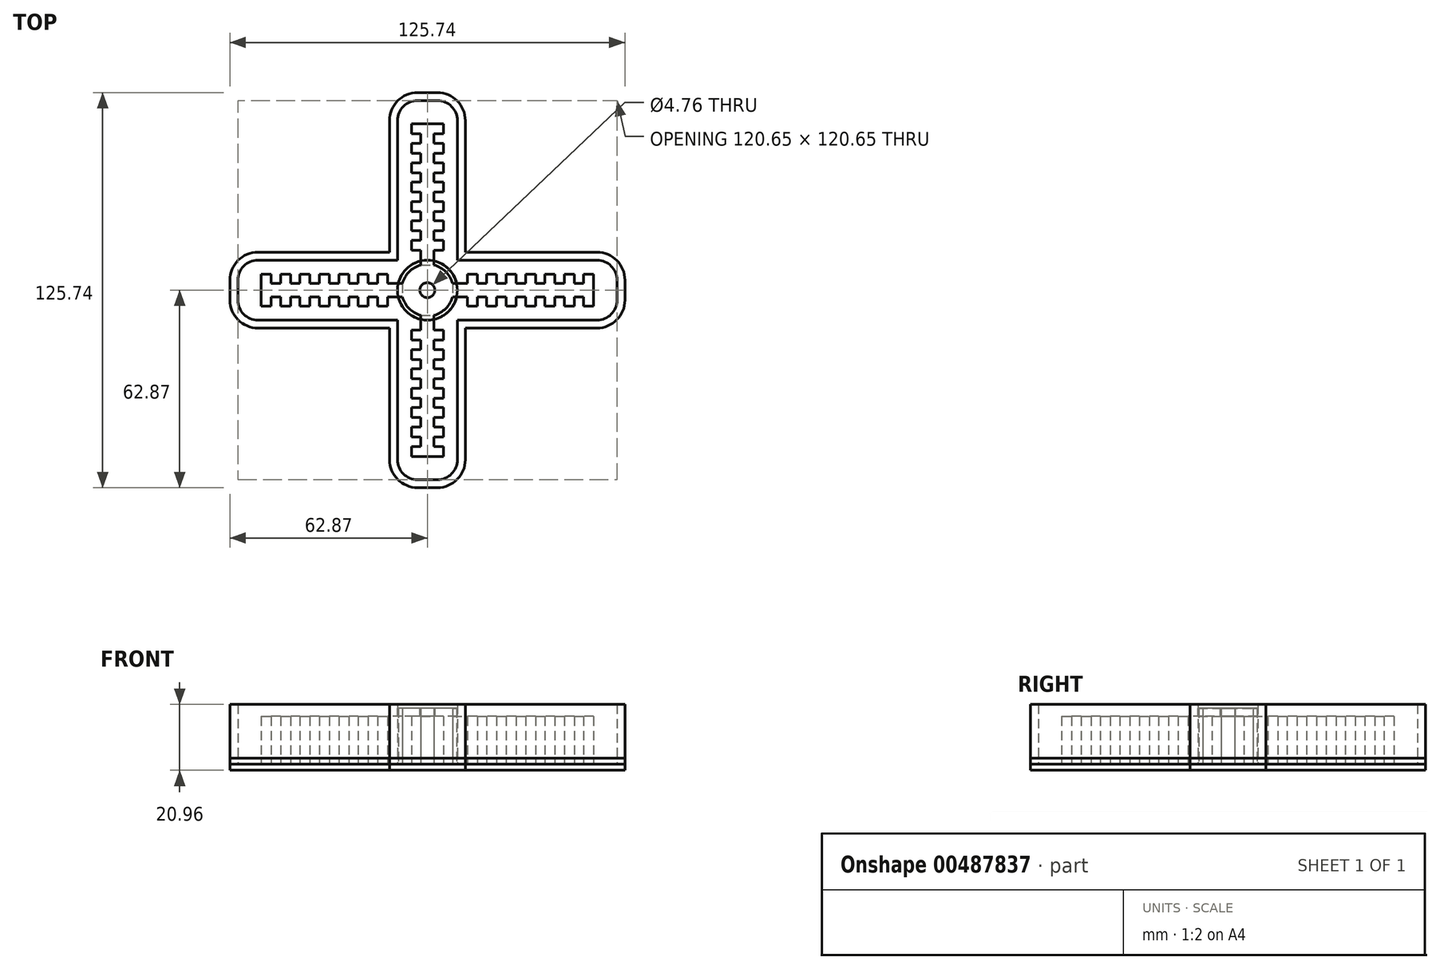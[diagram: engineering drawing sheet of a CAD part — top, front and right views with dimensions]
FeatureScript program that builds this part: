
annotation { "Feature Type Name" : "Feature", "Feature Type Description" : "" }
export const myFeature = defineFeature(function(context is Context, id is Id, definition is map)
    precondition{}
    {
        {
            var Q0;
            Q0=qCreatedBy(makeId("Top.planeOp"),FACE);
            var sketch = newSketch(context, id + "F0", { "sketchPlane" : qUnion([Q0])});
            skArc(sketch, "E0", {"start": v(-2.12, 9.29) * mm, "mid": v(-6.74, 6.74) * mm, "end": v(-9.29, 2.12) * mm});
            skLineSegment(sketch, "E1", {"start": v(-3.18, 60.33) * mm, "end": v(3.17, 60.33) * mm});
            skLineSegment(sketch, "E2.0", {"start": v(2.12, 7.98) * mm, "end": v(2.12, 12.7) * mm});
            skLineSegment(sketch, "E3.0", {"start": v(-2.12, 7.98) * mm, "end": v(-2.12, 12.7) * mm});
            skLineSegment(sketch, "E4", {"start": v(-5.08, 15.88) * mm, "end": v(-2.12, 15.88) * mm});
            skLineSegment(sketch, "E5", {"start": v(5.08, 15.88) * mm, "end": v(5.08, 12.7) * mm});
            skLineSegment(sketch, "E6", {"start": v(5.08, 12.7) * mm, "end": v(2.12, 12.7) * mm});
            skLineSegment(sketch, "E7", {"start": v(-5.08, 12.7) * mm, "end": v(-5.08, 15.88) * mm});
            skLineSegment(sketch, "E8.0.1.0", {"start": v(-5.08, 22.05) * mm, "end": v(-2.12, 22.05) * mm});
            skLineSegment(sketch, "E8.0.1.1", {"start": v(-5.08, 18.87) * mm, "end": v(-5.08, 22.05) * mm});
            skLineSegment(sketch, "E8.0.1.2", {"start": v(5.08, 18.87) * mm, "end": v(2.12, 18.87) * mm});
            skLineSegment(sketch, "E8.0.1.3", {"start": v(5.08, 22.05) * mm, "end": v(5.08, 18.87) * mm});
            skLineSegment(sketch, "E8.0.2.0", {"start": v(-5.08, 28.22) * mm, "end": v(-2.12, 28.22) * mm});
            skLineSegment(sketch, "E8.0.2.1", {"start": v(-5.08, 25.04) * mm, "end": v(-5.08, 28.22) * mm});
            skLineSegment(sketch, "E8.0.2.2", {"start": v(5.08, 25.04) * mm, "end": v(2.12, 25.04) * mm});
            skLineSegment(sketch, "E8.0.2.3", {"start": v(5.08, 28.22) * mm, "end": v(5.08, 25.04) * mm});
            skLineSegment(sketch, "E8.0.3.0", {"start": v(-5.08, 34.4) * mm, "end": v(-2.12, 34.4) * mm});
            skLineSegment(sketch, "E8.0.3.1", {"start": v(-5.08, 31.22) * mm, "end": v(-5.08, 34.4) * mm});
            skLineSegment(sketch, "E8.0.3.2", {"start": v(5.08, 31.22) * mm, "end": v(2.12, 31.22) * mm});
            skLineSegment(sketch, "E8.0.3.3", {"start": v(5.08, 34.4) * mm, "end": v(5.08, 31.22) * mm});
            skLineSegment(sketch, "E8.0.4.0", {"start": v(-5.08, 40.56) * mm, "end": v(-2.12, 40.56) * mm});
            skLineSegment(sketch, "E8.0.4.1", {"start": v(-5.08, 37.39) * mm, "end": v(-5.08, 40.56) * mm});
            skLineSegment(sketch, "E8.0.4.2", {"start": v(5.08, 37.39) * mm, "end": v(2.12, 37.39) * mm});
            skLineSegment(sketch, "E8.0.4.3", {"start": v(5.08, 40.56) * mm, "end": v(5.08, 37.39) * mm});
            skLineSegment(sketch, "E8.0.5.0", {"start": v(-5.08, 46.74) * mm, "end": v(-2.12, 46.74) * mm});
            skLineSegment(sketch, "E8.0.5.1", {"start": v(-5.08, 43.56) * mm, "end": v(-5.08, 46.74) * mm});
            skLineSegment(sketch, "E8.0.5.2", {"start": v(5.08, 43.56) * mm, "end": v(2.12, 43.56) * mm});
            skLineSegment(sketch, "E8.0.5.3", {"start": v(5.08, 46.74) * mm, "end": v(5.08, 43.56) * mm});
            skLineSegment(sketch, "E8.0.6.1", {"start": v(-5.08, 49.73) * mm, "end": v(-5.08, 52.9) * mm});
            skLineSegment(sketch, "E8.0.6.2", {"start": v(5.08, 49.73) * mm, "end": v(2.12, 49.73) * mm});
            skLineSegment(sketch, "E8.0.6.3", {"start": v(5.08, 52.9) * mm, "end": v(5.08, 49.73) * mm});
            skLineSegment(sketch, "E8.direction1", {"start": v(-5.08, 15.88) * mm, "end": v(-2.12, 15.88) * mm, "construction": true});
            skLineSegment(sketch, "E8.direction2", {"start": v(-5.08, 18.87) * mm, "end": v(-5.08, 22.05) * mm, "construction": true});
            skLineSegment(sketch, "E9.trimOffspring", {"start": v(-2.12, 12.7) * mm, "end": v(-5.08, 12.7) * mm});
            skLineSegment(sketch, "E10.trimOffspring", {"start": v(2.12, 15.88) * mm, "end": v(20.32, 15.88) * mm, "construction": true});
            skLineSegment(sketch, "E11.trimOffspring", {"start": v(2.12, 15.88) * mm, "end": v(5.08, 15.88) * mm});
            skLineSegment(sketch, "E12.trimOffspring", {"start": v(2.12, 15.88) * mm, "end": v(2.12, 18.87) * mm});
            skLineSegment(sketch, "E13.trimOffspring", {"start": v(-2.12, 15.88) * mm, "end": v(-2.12, 18.87) * mm});
            skLineSegment(sketch, "E14.trimOffspring", {"start": v(-2.12, 18.87) * mm, "end": v(-5.08, 18.87) * mm});
            skLineSegment(sketch, "E15.trimOffspring", {"start": v(2.12, 22.05) * mm, "end": v(2.12, 25.04) * mm});
            skLineSegment(sketch, "E16.trimOffspring", {"start": v(2.12, 22.05) * mm, "end": v(5.08, 22.05) * mm});
            skLineSegment(sketch, "E17.trimOffspring", {"start": v(-2.12, 22.05) * mm, "end": v(-2.12, 25.04) * mm});
            skLineSegment(sketch, "E18.trimOffspring", {"start": v(-2.12, 25.04) * mm, "end": v(-5.08, 25.04) * mm});
            skLineSegment(sketch, "E19.trimOffspring", {"start": v(-2.12, 28.22) * mm, "end": v(-2.12, 31.22) * mm});
            skLineSegment(sketch, "E20.trimOffspring", {"start": v(2.12, 28.22) * mm, "end": v(2.12, 31.22) * mm});
            skLineSegment(sketch, "E21.trimOffspring", {"start": v(2.12, 28.22) * mm, "end": v(5.08, 28.22) * mm});
            skLineSegment(sketch, "E22.trimOffspring", {"start": v(-2.12, 31.22) * mm, "end": v(-5.08, 31.22) * mm});
            skLineSegment(sketch, "E23.trimOffspring", {"start": v(2.12, 34.4) * mm, "end": v(5.08, 34.4) * mm});
            skLineSegment(sketch, "E24.trimOffspring", {"start": v(-2.12, 37.39) * mm, "end": v(-5.08, 37.39) * mm});
            skLineSegment(sketch, "E25.trimOffspring", {"start": v(2.12, 40.56) * mm, "end": v(5.08, 40.56) * mm});
            skLineSegment(sketch, "E26.trimOffspring", {"start": v(-2.12, 43.56) * mm, "end": v(-5.08, 43.56) * mm});
            skLineSegment(sketch, "E27.trimOffspring", {"start": v(2.12, 46.74) * mm, "end": v(5.08, 46.74) * mm});
            skLineSegment(sketch, "E28.trimOffspring", {"start": v(-2.12, 49.73) * mm, "end": v(-5.08, 49.73) * mm});
            skLineSegment(sketch, "E29.trimOffspring", {"start": v(-2.12, 46.74) * mm, "end": v(-2.12, 49.73) * mm});
            skLineSegment(sketch, "E30.trimOffspring", {"start": v(2.12, 46.74) * mm, "end": v(2.12, 49.73) * mm});
            skLineSegment(sketch, "E31.trimOffspring", {"start": v(-2.12, 40.56) * mm, "end": v(-2.12, 43.56) * mm});
            skLineSegment(sketch, "E32.trimOffspring", {"start": v(2.12, 40.56) * mm, "end": v(2.12, 43.56) * mm});
            skLineSegment(sketch, "E33.trimOffspring", {"start": v(-2.12, 34.4) * mm, "end": v(-2.12, 37.39) * mm});
            skLineSegment(sketch, "E34.trimOffspring", {"start": v(2.12, 34.4) * mm, "end": v(2.12, 37.39) * mm});
            skLineSegment(sketch, "E35", {"start": v(5.08, 52.9) * mm, "end": v(-5.08, 52.9) * mm});
            skLineSegment(sketch, "E36.1.0", {"start": v(-15.88, 2.12) * mm, "end": v(-18.87, 2.12) * mm});
            skLineSegment(sketch, "E36.1.1", {"start": v(-22.05, -5.08) * mm, "end": v(-22.05, -2.12) * mm});
            skLineSegment(sketch, "E36.1.2", {"start": v(-28.22, -5.08) * mm, "end": v(-28.22, -2.12) * mm});
            skLineSegment(sketch, "E36.1.3", {"start": v(-28.22, 2.12) * mm, "end": v(-28.22, 5.08) * mm});
            skLineSegment(sketch, "E36.1.4", {"start": v(-49.73, 5.08) * mm, "end": v(-49.73, 2.12) * mm});
            skLineSegment(sketch, "E36.1.5", {"start": v(-40.56, -5.08) * mm, "end": v(-40.56, -2.12) * mm});
            skLineSegment(sketch, "E36.1.6", {"start": v(-49.73, -2.12) * mm, "end": v(-49.73, -5.08) * mm});
            skLineSegment(sketch, "E36.1.7", {"start": v(-46.74, -2.12) * mm, "end": v(-49.73, -2.12) * mm});
            skLineSegment(sketch, "E36.1.8", {"start": v(-18.87, 5.08) * mm, "end": v(-18.87, 2.12) * mm});
            skLineSegment(sketch, "E36.1.9", {"start": v(-49.73, -5.08) * mm, "end": v(-52.9, -5.08) * mm});
            skLineSegment(sketch, "E36.1.10", {"start": v(-15.88, 2.12) * mm, "end": v(-15.88, 5.08) * mm});
            skLineSegment(sketch, "E36.1.11", {"start": v(-12.7, -5.08) * mm, "end": v(-15.88, -5.08) * mm});
            skLineSegment(sketch, "E36.1.12", {"start": v(-28.22, 2.12) * mm, "end": v(-31.22, 2.12) * mm});
            skLineSegment(sketch, "E36.1.13", {"start": v(-12.7, 5.08) * mm, "end": v(-12.7, 2.12) * mm});
            skLineSegment(sketch, "E36.1.14", {"start": v(-15.88, 5.08) * mm, "end": v(-12.7, 5.08) * mm});
            skLineSegment(sketch, "E36.1.15", {"start": v(-25.04, 5.08) * mm, "end": v(-25.04, 2.12) * mm});
            skLineSegment(sketch, "E36.1.16", {"start": v(-15.88, -2.12) * mm, "end": v(-18.87, -2.12) * mm});
            skLineSegment(sketch, "E36.1.17", {"start": v(-25.04, -2.12) * mm, "end": v(-25.04, -5.08) * mm});
            skLineSegment(sketch, "E36.1.18", {"start": v(-43.56, 5.08) * mm, "end": v(-43.56, 2.12) * mm});
            skLineSegment(sketch, "E36.1.19", {"start": v(-46.74, 2.12) * mm, "end": v(-46.74, 5.08) * mm});
            skLineSegment(sketch, "E36.1.20", {"start": v(-37.39, -5.08) * mm, "end": v(-40.56, -5.08) * mm});
            skLineSegment(sketch, "E36.1.21", {"start": v(-22.05, 5.08) * mm, "end": v(-18.87, 5.08) * mm});
            skLineSegment(sketch, "E36.1.22", {"start": v(-34.4, 5.08) * mm, "end": v(-31.22, 5.08) * mm});
            skLineSegment(sketch, "E36.1.23", {"start": v(-25.04, -5.08) * mm, "end": v(-28.22, -5.08) * mm});
            skLineSegment(sketch, "E36.1.24", {"start": v(-34.4, 2.12) * mm, "end": v(-37.39, 2.12) * mm});
            skLineSegment(sketch, "E36.1.25", {"start": v(-46.74, 5.08) * mm, "end": v(-43.56, 5.08) * mm});
            skLineSegment(sketch, "E36.1.26", {"start": v(-43.56, -2.12) * mm, "end": v(-43.56, -5.08) * mm});
            skLineSegment(sketch, "E36.1.27", {"start": v(-28.22, -2.12) * mm, "end": v(-31.22, -2.12) * mm});
            skLineSegment(sketch, "E36.1.28", {"start": v(-52.9, 5.08) * mm, "end": v(-52.9, -5.08) * mm});
            skLineSegment(sketch, "E36.1.29", {"start": v(-31.22, 5.08) * mm, "end": v(-31.22, 2.12) * mm});
            skLineSegment(sketch, "E36.1.30", {"start": v(-15.88, -5.08) * mm, "end": v(-22.05, -5.08) * mm, "construction": true});
            skLineSegment(sketch, "E36.1.31", {"start": v(-37.39, -2.12) * mm, "end": v(-37.39, -5.08) * mm});
            skLineSegment(sketch, "E36.1.32", {"start": v(-43.56, -5.08) * mm, "end": v(-46.74, -5.08) * mm});
            skLineSegment(sketch, "E36.1.33", {"start": v(-34.4, -5.08) * mm, "end": v(-34.4, -2.12) * mm});
            skLineSegment(sketch, "E36.1.34", {"start": v(-22.05, -2.12) * mm, "end": v(-25.04, -2.12) * mm});
            skLineSegment(sketch, "E36.1.35", {"start": v(-34.4, -2.12) * mm, "end": v(-37.39, -2.12) * mm});
            skLineSegment(sketch, "E36.1.36", {"start": v(-40.56, 5.08) * mm, "end": v(-37.39, 5.08) * mm});
            skLineSegment(sketch, "E36.1.37", {"start": v(-22.05, 2.12) * mm, "end": v(-25.04, 2.12) * mm});
            skLineSegment(sketch, "E36.1.38", {"start": v(-40.56, -2.12) * mm, "end": v(-43.56, -2.12) * mm});
            skLineSegment(sketch, "E36.1.39", {"start": v(-15.88, -5.08) * mm, "end": v(-15.88, -2.12) * mm, "construction": true});
            skLineSegment(sketch, "E36.1.40", {"start": v(-12.7, -2.12) * mm, "end": v(-12.7, -5.08) * mm});
            skLineSegment(sketch, "E36.1.41", {"start": v(-34.4, 2.12) * mm, "end": v(-34.4, 5.08) * mm});
            skLineSegment(sketch, "E36.1.42", {"start": v(-28.22, 5.08) * mm, "end": v(-25.04, 5.08) * mm});
            skLineSegment(sketch, "E36.1.43", {"start": v(-40.56, 2.12) * mm, "end": v(-40.56, 5.08) * mm});
            skLineSegment(sketch, "E36.1.44", {"start": v(-37.39, 5.08) * mm, "end": v(-37.39, 2.12) * mm});
            skLineSegment(sketch, "E36.1.45", {"start": v(-18.87, -2.12) * mm, "end": v(-18.87, -5.08) * mm});
            skLineSegment(sketch, "E36.1.46", {"start": v(-46.74, 2.12) * mm, "end": v(-49.73, 2.12) * mm});
            skLineSegment(sketch, "E36.1.47", {"start": v(-31.22, -5.08) * mm, "end": v(-34.4, -5.08) * mm});
            skLineSegment(sketch, "E36.1.48", {"start": v(-46.74, -5.08) * mm, "end": v(-46.74, -2.12) * mm});
            skLineSegment(sketch, "E36.1.49", {"start": v(-22.05, 2.12) * mm, "end": v(-22.05, 5.08) * mm});
            skLineSegment(sketch, "E36.1.50", {"start": v(-40.56, 2.12) * mm, "end": v(-43.56, 2.12) * mm});
            skLineSegment(sketch, "E36.1.51", {"start": v(-52.9, 5.08) * mm, "end": v(-49.73, 5.08) * mm});
            skLineSegment(sketch, "E36.1.52", {"start": v(-31.22, -2.12) * mm, "end": v(-31.22, -5.08) * mm});
            skLineSegment(sketch, "E36.1.53", {"start": v(-18.87, -5.08) * mm, "end": v(-22.05, -5.08) * mm});
            skLineSegment(sketch, "E36.1.54", {"start": v(-15.88, -5.08) * mm, "end": v(-15.88, -2.12) * mm});
            skLineSegment(sketch, "E36.1.55", {"start": v(-7.98, -2.12) * mm, "end": v(-12.7, -2.12) * mm});
            skLineSegment(sketch, "E36.1.56", {"start": v(-7.98, 2.12) * mm, "end": v(-12.7, 2.12) * mm});
            skLineSegment(sketch, "E36.1.58", {"start": v(-60.33, -3.18) * mm, "end": v(-60.33, 3.17) * mm});
            skLineSegment(sketch, "E36.2.0", {"start": v(-2.12, -15.88) * mm, "end": v(-2.12, -18.87) * mm});
            skLineSegment(sketch, "E36.2.1", {"start": v(5.08, -22.05) * mm, "end": v(2.12, -22.05) * mm});
            skLineSegment(sketch, "E36.2.2", {"start": v(5.08, -28.22) * mm, "end": v(2.12, -28.22) * mm});
            skLineSegment(sketch, "E36.2.3", {"start": v(-2.12, -28.22) * mm, "end": v(-5.08, -28.22) * mm});
            skLineSegment(sketch, "E36.2.4", {"start": v(-5.08, -49.73) * mm, "end": v(-2.12, -49.73) * mm});
            skLineSegment(sketch, "E36.2.5", {"start": v(5.08, -40.56) * mm, "end": v(2.12, -40.56) * mm});
            skLineSegment(sketch, "E36.2.6", {"start": v(2.12, -49.73) * mm, "end": v(5.08, -49.73) * mm});
            skLineSegment(sketch, "E36.2.7", {"start": v(2.12, -46.74) * mm, "end": v(2.12, -49.73) * mm});
            skLineSegment(sketch, "E36.2.8", {"start": v(-5.08, -18.87) * mm, "end": v(-2.12, -18.87) * mm});
            skLineSegment(sketch, "E36.2.9", {"start": v(5.08, -49.73) * mm, "end": v(5.08, -52.9) * mm});
            skLineSegment(sketch, "E36.2.10", {"start": v(-2.12, -15.88) * mm, "end": v(-5.08, -15.88) * mm});
            skLineSegment(sketch, "E36.2.11", {"start": v(5.08, -12.7) * mm, "end": v(5.08, -15.88) * mm});
            skLineSegment(sketch, "E36.2.12", {"start": v(-2.12, -28.22) * mm, "end": v(-2.12, -31.22) * mm});
            skLineSegment(sketch, "E36.2.13", {"start": v(-5.08, -12.7) * mm, "end": v(-2.12, -12.7) * mm});
            skLineSegment(sketch, "E36.2.14", {"start": v(-5.08, -15.88) * mm, "end": v(-5.08, -12.7) * mm});
            skLineSegment(sketch, "E36.2.15", {"start": v(-5.08, -25.04) * mm, "end": v(-2.12, -25.04) * mm});
            skLineSegment(sketch, "E36.2.16", {"start": v(2.12, -15.88) * mm, "end": v(2.12, -18.87) * mm});
            skLineSegment(sketch, "E36.2.17", {"start": v(2.12, -25.04) * mm, "end": v(5.08, -25.04) * mm});
            skLineSegment(sketch, "E36.2.18", {"start": v(-5.08, -43.56) * mm, "end": v(-2.12, -43.56) * mm});
            skLineSegment(sketch, "E36.2.19", {"start": v(-2.12, -46.74) * mm, "end": v(-5.08, -46.74) * mm});
            skLineSegment(sketch, "E36.2.20", {"start": v(5.08, -37.39) * mm, "end": v(5.08, -40.56) * mm});
            skLineSegment(sketch, "E36.2.21", {"start": v(-5.08, -22.05) * mm, "end": v(-5.08, -18.87) * mm});
            skLineSegment(sketch, "E36.2.22", {"start": v(-5.08, -34.4) * mm, "end": v(-5.08, -31.22) * mm});
            skLineSegment(sketch, "E36.2.23", {"start": v(5.08, -25.04) * mm, "end": v(5.08, -28.22) * mm});
            skLineSegment(sketch, "E36.2.24", {"start": v(-2.12, -34.4) * mm, "end": v(-2.12, -37.39) * mm});
            skLineSegment(sketch, "E36.2.25", {"start": v(-5.08, -46.74) * mm, "end": v(-5.08, -43.56) * mm});
            skLineSegment(sketch, "E36.2.26", {"start": v(2.12, -43.56) * mm, "end": v(5.08, -43.56) * mm});
            skLineSegment(sketch, "E36.2.27", {"start": v(2.12, -28.22) * mm, "end": v(2.12, -31.22) * mm});
            skLineSegment(sketch, "E36.2.28", {"start": v(-5.08, -52.9) * mm, "end": v(5.08, -52.9) * mm});
            skLineSegment(sketch, "E36.2.29", {"start": v(-5.08, -31.22) * mm, "end": v(-2.12, -31.22) * mm});
            skLineSegment(sketch, "E36.2.30", {"start": v(5.08, -15.88) * mm, "end": v(5.08, -22.05) * mm, "construction": true});
            skLineSegment(sketch, "E36.2.31", {"start": v(2.12, -37.39) * mm, "end": v(5.08, -37.39) * mm});
            skLineSegment(sketch, "E36.2.32", {"start": v(5.08, -43.56) * mm, "end": v(5.08, -46.74) * mm});
            skLineSegment(sketch, "E36.2.33", {"start": v(5.08, -34.4) * mm, "end": v(2.12, -34.4) * mm});
            skLineSegment(sketch, "E36.2.34", {"start": v(2.12, -22.05) * mm, "end": v(2.12, -25.04) * mm});
            skLineSegment(sketch, "E36.2.35", {"start": v(2.12, -34.4) * mm, "end": v(2.12, -37.39) * mm});
            skLineSegment(sketch, "E36.2.36", {"start": v(-5.08, -40.56) * mm, "end": v(-5.08, -37.39) * mm});
            skLineSegment(sketch, "E36.2.37", {"start": v(-2.12, -22.05) * mm, "end": v(-2.12, -25.04) * mm});
            skLineSegment(sketch, "E36.2.38", {"start": v(2.12, -40.56) * mm, "end": v(2.12, -43.56) * mm});
            skLineSegment(sketch, "E36.2.39", {"start": v(5.08, -15.88) * mm, "end": v(2.12, -15.88) * mm, "construction": true});
            skLineSegment(sketch, "E36.2.40", {"start": v(2.12, -12.7) * mm, "end": v(5.08, -12.7) * mm});
            skLineSegment(sketch, "E36.2.41", {"start": v(-2.12, -34.4) * mm, "end": v(-5.08, -34.4) * mm});
            skLineSegment(sketch, "E36.2.42", {"start": v(-5.08, -28.22) * mm, "end": v(-5.08, -25.04) * mm});
            skLineSegment(sketch, "E36.2.43", {"start": v(-2.12, -40.56) * mm, "end": v(-5.08, -40.56) * mm});
            skLineSegment(sketch, "E36.2.44", {"start": v(-5.08, -37.39) * mm, "end": v(-2.12, -37.39) * mm});
            skLineSegment(sketch, "E36.2.45", {"start": v(2.12, -18.87) * mm, "end": v(5.08, -18.87) * mm});
            skLineSegment(sketch, "E36.2.46", {"start": v(-2.12, -46.74) * mm, "end": v(-2.12, -49.73) * mm});
            skLineSegment(sketch, "E36.2.47", {"start": v(5.08, -31.22) * mm, "end": v(5.08, -34.4) * mm});
            skLineSegment(sketch, "E36.2.48", {"start": v(5.08, -46.74) * mm, "end": v(2.12, -46.74) * mm});
            skLineSegment(sketch, "E36.2.49", {"start": v(-2.12, -22.05) * mm, "end": v(-5.08, -22.05) * mm});
            skLineSegment(sketch, "E36.2.50", {"start": v(-2.12, -40.56) * mm, "end": v(-2.12, -43.56) * mm});
            skLineSegment(sketch, "E36.2.51", {"start": v(-5.08, -52.9) * mm, "end": v(-5.08, -49.73) * mm});
            skLineSegment(sketch, "E36.2.52", {"start": v(2.12, -31.22) * mm, "end": v(5.08, -31.22) * mm});
            skLineSegment(sketch, "E36.2.53", {"start": v(5.08, -18.87) * mm, "end": v(5.08, -22.05) * mm});
            skLineSegment(sketch, "E36.2.54", {"start": v(5.08, -15.88) * mm, "end": v(2.12, -15.88) * mm});
            skLineSegment(sketch, "E36.2.55", {"start": v(2.12, -7.98) * mm, "end": v(2.12, -12.7) * mm});
            skLineSegment(sketch, "E36.2.56", {"start": v(-2.12, -7.98) * mm, "end": v(-2.12, -12.7) * mm});
            skLineSegment(sketch, "E36.2.58", {"start": v(3.17, -60.33) * mm, "end": v(-3.18, -60.33) * mm});
            skLineSegment(sketch, "E36.3.0", {"start": v(15.88, -2.12) * mm, "end": v(18.87, -2.12) * mm});
            skLineSegment(sketch, "E36.3.1", {"start": v(22.05, 5.08) * mm, "end": v(22.05, 2.12) * mm});
            skLineSegment(sketch, "E36.3.2", {"start": v(28.22, 5.08) * mm, "end": v(28.22, 2.12) * mm});
            skLineSegment(sketch, "E36.3.3", {"start": v(28.22, -2.12) * mm, "end": v(28.22, -5.08) * mm});
            skLineSegment(sketch, "E36.3.4", {"start": v(49.73, -5.08) * mm, "end": v(49.73, -2.12) * mm});
            skLineSegment(sketch, "E36.3.5", {"start": v(40.56, 5.08) * mm, "end": v(40.56, 2.12) * mm});
            skLineSegment(sketch, "E36.3.6", {"start": v(49.73, 2.12) * mm, "end": v(49.73, 5.08) * mm});
            skLineSegment(sketch, "E36.3.7", {"start": v(46.74, 2.12) * mm, "end": v(49.73, 2.12) * mm});
            skLineSegment(sketch, "E36.3.8", {"start": v(18.87, -5.08) * mm, "end": v(18.87, -2.12) * mm});
            skLineSegment(sketch, "E36.3.9", {"start": v(49.73, 5.08) * mm, "end": v(52.9, 5.08) * mm});
            skLineSegment(sketch, "E36.3.10", {"start": v(15.88, -2.12) * mm, "end": v(15.88, -5.08) * mm});
            skLineSegment(sketch, "E36.3.11", {"start": v(12.7, 5.08) * mm, "end": v(15.88, 5.08) * mm});
            skLineSegment(sketch, "E36.3.12", {"start": v(28.22, -2.12) * mm, "end": v(31.22, -2.12) * mm});
            skLineSegment(sketch, "E36.3.13", {"start": v(12.7, -5.08) * mm, "end": v(12.7, -2.12) * mm});
            skLineSegment(sketch, "E36.3.14", {"start": v(15.88, -5.08) * mm, "end": v(12.7, -5.08) * mm});
            skLineSegment(sketch, "E36.3.15", {"start": v(25.04, -5.08) * mm, "end": v(25.04, -2.12) * mm});
            skLineSegment(sketch, "E36.3.16", {"start": v(15.88, 2.12) * mm, "end": v(18.87, 2.12) * mm});
            skLineSegment(sketch, "E36.3.17", {"start": v(25.04, 2.12) * mm, "end": v(25.04, 5.08) * mm});
            skLineSegment(sketch, "E36.3.18", {"start": v(43.56, -5.08) * mm, "end": v(43.56, -2.12) * mm});
            skLineSegment(sketch, "E36.3.19", {"start": v(46.74, -2.12) * mm, "end": v(46.74, -5.08) * mm});
            skLineSegment(sketch, "E36.3.20", {"start": v(37.39, 5.08) * mm, "end": v(40.56, 5.08) * mm});
            skLineSegment(sketch, "E36.3.21", {"start": v(22.05, -5.08) * mm, "end": v(18.87, -5.08) * mm});
            skLineSegment(sketch, "E36.3.22", {"start": v(34.4, -5.08) * mm, "end": v(31.22, -5.08) * mm});
            skLineSegment(sketch, "E36.3.23", {"start": v(25.04, 5.08) * mm, "end": v(28.22, 5.08) * mm});
            skLineSegment(sketch, "E36.3.24", {"start": v(34.4, -2.12) * mm, "end": v(37.39, -2.12) * mm});
            skLineSegment(sketch, "E36.3.25", {"start": v(46.74, -5.08) * mm, "end": v(43.56, -5.08) * mm});
            skLineSegment(sketch, "E36.3.26", {"start": v(43.56, 2.12) * mm, "end": v(43.56, 5.08) * mm});
            skLineSegment(sketch, "E36.3.27", {"start": v(28.22, 2.12) * mm, "end": v(31.22, 2.12) * mm});
            skLineSegment(sketch, "E36.3.28", {"start": v(52.9, -5.08) * mm, "end": v(52.9, 5.08) * mm});
            skLineSegment(sketch, "E36.3.29", {"start": v(31.22, -5.08) * mm, "end": v(31.22, -2.12) * mm});
            skLineSegment(sketch, "E36.3.31", {"start": v(37.39, 2.12) * mm, "end": v(37.39, 5.08) * mm});
            skLineSegment(sketch, "E36.3.32", {"start": v(43.56, 5.08) * mm, "end": v(46.74, 5.08) * mm});
            skLineSegment(sketch, "E36.3.33", {"start": v(34.4, 5.08) * mm, "end": v(34.4, 2.12) * mm});
            skLineSegment(sketch, "E36.3.34", {"start": v(22.05, 2.12) * mm, "end": v(25.04, 2.12) * mm});
            skLineSegment(sketch, "E36.3.35", {"start": v(34.4, 2.12) * mm, "end": v(37.39, 2.12) * mm});
            skLineSegment(sketch, "E36.3.36", {"start": v(40.56, -5.08) * mm, "end": v(37.39, -5.08) * mm});
            skLineSegment(sketch, "E36.3.37", {"start": v(22.05, -2.12) * mm, "end": v(25.04, -2.12) * mm});
            skLineSegment(sketch, "E36.3.38", {"start": v(40.56, 2.12) * mm, "end": v(43.56, 2.12) * mm});
            skLineSegment(sketch, "E36.3.39", {"start": v(15.88, 5.08) * mm, "end": v(15.88, 2.12) * mm, "construction": true});
            skLineSegment(sketch, "E36.3.40", {"start": v(12.7, 2.12) * mm, "end": v(12.7, 5.08) * mm});
            skLineSegment(sketch, "E36.3.41", {"start": v(34.4, -2.12) * mm, "end": v(34.4, -5.08) * mm});
            skLineSegment(sketch, "E36.3.42", {"start": v(28.22, -5.08) * mm, "end": v(25.04, -5.08) * mm});
            skLineSegment(sketch, "E36.3.43", {"start": v(40.56, -2.12) * mm, "end": v(40.56, -5.08) * mm});
            skLineSegment(sketch, "E36.3.44", {"start": v(37.39, -5.08) * mm, "end": v(37.39, -2.12) * mm});
            skLineSegment(sketch, "E36.3.45", {"start": v(18.87, 2.12) * mm, "end": v(18.87, 5.08) * mm});
            skLineSegment(sketch, "E36.3.46", {"start": v(46.74, -2.12) * mm, "end": v(49.73, -2.12) * mm});
            skLineSegment(sketch, "E36.3.47", {"start": v(31.22, 5.08) * mm, "end": v(34.4, 5.08) * mm});
            skLineSegment(sketch, "E36.3.48", {"start": v(46.74, 5.08) * mm, "end": v(46.74, 2.12) * mm});
            skLineSegment(sketch, "E36.3.49", {"start": v(22.05, -2.12) * mm, "end": v(22.05, -5.08) * mm});
            skLineSegment(sketch, "E36.3.50", {"start": v(40.56, -2.12) * mm, "end": v(43.56, -2.12) * mm});
            skLineSegment(sketch, "E36.3.51", {"start": v(52.9, -5.08) * mm, "end": v(49.73, -5.08) * mm});
            skLineSegment(sketch, "E36.3.52", {"start": v(31.22, 2.12) * mm, "end": v(31.22, 5.08) * mm});
            skLineSegment(sketch, "E36.3.53", {"start": v(18.87, 5.08) * mm, "end": v(22.05, 5.08) * mm});
            skLineSegment(sketch, "E36.3.54", {"start": v(15.88, 5.08) * mm, "end": v(15.88, 2.12) * mm});
            skLineSegment(sketch, "E36.3.55", {"start": v(7.98, 2.12) * mm, "end": v(12.7, 2.12) * mm});
            skLineSegment(sketch, "E36.3.56", {"start": v(7.98, -2.12) * mm, "end": v(12.7, -2.12) * mm});
            skLineSegment(sketch, "E36.3.58", {"start": v(60.32, 3.17) * mm, "end": v(60.32, -3.18) * mm});
            skLineSegment(sketch, "E37.trimOffspring", {"start": v(-9.53, 9.52) * mm, "end": v(-9.53, 53.98) * mm});
            skLineSegment(sketch, "E38.trimOffspring", {"start": v(-9.53, 9.52) * mm, "end": v(-53.98, 9.53) * mm});
            skLineSegment(sketch, "E39.trimOffspring", {"start": v(9.52, 9.53) * mm, "end": v(53.97, 9.52) * mm});
            skLineSegment(sketch, "E40.trimOffspring", {"start": v(9.52, 9.53) * mm, "end": v(9.52, 53.98) * mm});
            skLineSegment(sketch, "E41.trimOffspring", {"start": v(9.53, -9.52) * mm, "end": v(9.52, -53.98) * mm});
            skLineSegment(sketch, "E42.trimOffspring", {"start": v(9.53, -9.52) * mm, "end": v(53.98, -9.53) * mm});
            skLineSegment(sketch, "E43.trimOffspring", {"start": v(-9.52, -9.53) * mm, "end": v(-9.53, -53.98) * mm});
            skLineSegment(sketch, "E44.trimOffspring", {"start": v(-9.52, -9.53) * mm, "end": v(-53.98, -9.53) * mm});
            skArc(sketch, "E45.trimOffspring", {"start": v(-9.29, -2.12) * mm, "mid": v(-6.74, -6.74) * mm, "end": v(-2.12, -9.29) * mm});
            skArc(sketch, "E46.trimOffspring", {"start": v(9.29, 2.12) * mm, "mid": v(6.74, 6.74) * mm, "end": v(2.12, 9.29) * mm});
            skArc(sketch, "E47.trimOffspring", {"start": v(2.12, -9.29) * mm, "mid": v(6.74, -6.74) * mm, "end": v(9.29, -2.12) * mm});
            skPoint(sketch, "E48.visualSharp", {"position": v(60.32, -9.53) * mm});
            skArc(sketch, "E48.filletArc", {"start": v(53.98, -9.53) * mm, "mid": v(58.47, -7.67) * mm, "end": v(60.32, -3.18) * mm});
            skPoint(sketch, "E49.visualSharp", {"position": v(60.33, 9.52) * mm});
            skArc(sketch, "E49.filletArc", {"start": v(60.32, 3.17) * mm, "mid": v(58.47, 7.67) * mm, "end": v(53.97, 9.52) * mm});
            skPoint(sketch, "E50.visualSharp", {"position": v(9.52, 60.33) * mm});
            skArc(sketch, "E50.filletArc", {"start": v(9.52, 53.98) * mm, "mid": v(7.67, 58.47) * mm, "end": v(3.17, 60.33) * mm});
            skPoint(sketch, "E51.visualSharp", {"position": v(-9.53, 60.33) * mm});
            skArc(sketch, "E51.filletArc", {"start": v(-3.18, 60.33) * mm, "mid": v(-7.67, 58.47) * mm, "end": v(-9.53, 53.98) * mm});
            skPoint(sketch, "E52.visualSharp", {"position": v(-60.33, 9.53) * mm});
            skArc(sketch, "E52.filletArc", {"start": v(-53.98, 9.52) * mm, "mid": v(-58.47, 7.67) * mm, "end": v(-60.33, 3.17) * mm});
            skPoint(sketch, "E53.visualSharp", {"position": v(-60.33, -9.53) * mm});
            skArc(sketch, "E53.filletArc", {"start": v(-60.33, -3.18) * mm, "mid": v(-58.47, -7.67) * mm, "end": v(-53.98, -9.53) * mm});
            skPoint(sketch, "E54.visualSharp", {"position": v(-9.53, -60.33) * mm});
            skArc(sketch, "E54.filletArc", {"start": v(-9.53, -53.98) * mm, "mid": v(-7.67, -58.47) * mm, "end": v(-3.18, -60.33) * mm});
            skPoint(sketch, "E55.visualSharp", {"position": v(9.52, -60.33) * mm});
            skArc(sketch, "E55.filletArc", {"start": v(3.17, -60.33) * mm, "mid": v(7.67, -58.47) * mm, "end": v(9.53, -53.98) * mm});
            skLineSegment(sketch, "E56.0", {"start": v(12.06, 12.07) * mm, "end": v(53.98, 12.06) * mm});
            skArc(sketch, "E56.1", {"start": v(62.87, 3.17) * mm, "mid": v(60.26, 9.46) * mm, "end": v(53.98, 12.06) * mm});
            skLineSegment(sketch, "E56.2", {"start": v(62.87, 3.17) * mm, "end": v(62.87, -3.18) * mm});
            skArc(sketch, "E56.3", {"start": v(53.97, -12.07) * mm, "mid": v(60.26, -9.46) * mm, "end": v(62.87, -3.18) * mm});
            skLineSegment(sketch, "E56.4", {"start": v(12.07, -12.07) * mm, "end": v(53.97, -12.07) * mm});
            skLineSegment(sketch, "E56.5", {"start": v(12.06, 12.07) * mm, "end": v(12.06, 53.98) * mm});
            skLineSegment(sketch, "E56.6", {"start": v(12.07, -12.07) * mm, "end": v(12.07, -53.98) * mm});
            skArc(sketch, "E56.7", {"start": v(3.17, -62.87) * mm, "mid": v(9.46, -60.26) * mm, "end": v(12.07, -53.98) * mm});
            skLineSegment(sketch, "E56.8", {"start": v(3.17, -62.87) * mm, "end": v(-3.18, -62.87) * mm});
            skArc(sketch, "E56.9", {"start": v(-12.07, -53.98) * mm, "mid": v(-9.46, -60.26) * mm, "end": v(-3.18, -62.87) * mm});
            skLineSegment(sketch, "E56.10", {"start": v(-12.07, 12.06) * mm, "end": v(-12.07, 53.98) * mm});
            skArc(sketch, "E56.11", {"start": v(-3.18, 62.87) * mm, "mid": v(-9.46, 60.26) * mm, "end": v(-12.07, 53.98) * mm});
            skLineSegment(sketch, "E56.12", {"start": v(-3.18, 62.87) * mm, "end": v(3.17, 62.87) * mm});
            skArc(sketch, "E56.13", {"start": v(12.06, 53.98) * mm, "mid": v(9.46, 60.26) * mm, "end": v(3.17, 62.87) * mm});
            skLineSegment(sketch, "E56.14", {"start": v(-12.07, 12.06) * mm, "end": v(-53.98, 12.07) * mm});
            skArc(sketch, "E56.15", {"start": v(-53.98, 12.07) * mm, "mid": v(-60.26, 9.46) * mm, "end": v(-62.87, 3.18) * mm});
            skLineSegment(sketch, "E56.16", {"start": v(-62.87, -3.18) * mm, "end": v(-62.87, 3.18) * mm});
            skArc(sketch, "E56.17", {"start": v(-62.87, -3.18) * mm, "mid": v(-60.26, -9.46) * mm, "end": v(-53.98, -12.07) * mm});
            skLineSegment(sketch, "E56.18", {"start": v(-12.06, -12.07) * mm, "end": v(-53.98, -12.07) * mm});
            skLineSegment(sketch, "E56.19", {"start": v(-12.06, -12.07) * mm, "end": v(-12.07, -53.98) * mm});
            skArc(sketch, "E57", {"start": v(-7.98, -2.12) * mm, "mid": v(-5.84, -5.84) * mm, "end": v(-2.12, -7.98) * mm});
            skArc(sketch, "E58.trimOffspring", {"start": v(2.12, -7.98) * mm, "mid": v(5.84, -5.84) * mm, "end": v(7.98, -2.12) * mm});
            skArc(sketch, "E59.trimOffspring", {"start": v(7.98, 2.12) * mm, "mid": v(5.84, 5.84) * mm, "end": v(2.12, 7.98) * mm});
            skArc(sketch, "E60.trimOffspring", {"start": v(-2.12, 7.98) * mm, "mid": v(-5.84, 5.84) * mm, "end": v(-7.98, 2.12) * mm});
            skLineSegment(sketch, "E61", {"start": v(-7.98, 2.12) * mm, "end": v(-7.98, -2.12) * mm});
            skLineSegment(sketch, "E62", {"start": v(-2.12, -7.98) * mm, "end": v(2.12, -7.98) * mm});
            skLineSegment(sketch, "E63", {"start": v(7.98, 2.12) * mm, "end": v(7.98, -2.12) * mm});
            skLineSegment(sketch, "E64", {"start": v(-2.12, 7.98) * mm, "end": v(2.12, 7.98) * mm});
            skSolve(sketch);
        }
        {
            var Q0;
            Q0=makeQuery(id+"F0.imprint","IMPRINT",FACE,{"disambiguationData":[TD([[makeQuery(id+"F0.imprint","IMPRINT",EDGE,{"derivedFrom":sQuery(id+"F0.wireOp",EDGE,"E1")}),1.0]])]});
            extrude(context, id + "F1", {"entities" : qUnion([Q0]), "depth" : 19.05 * mm});
        }
        {
            var Q0;
            Q0=makeQuery(id+"F0.imprint","IMPRINT",FACE,{"disambiguationData":[TD([[makeQuery(id+"F0.imprint","IMPRINT",EDGE,{"derivedFrom":sQuery(id+"F0.wireOp",EDGE,"E36.1.0")}),1.0]])]});
            var Q1;
            Q1=makeQuery(id+"F0.imprint","IMPRINT",FACE,{"disambiguationData":[TD([[makeQuery(id+"F0.imprint","IMPRINT",EDGE,{"derivedFrom":sQuery(id+"F0.wireOp",EDGE,"E4")}),-1.0]])]});
            var Q2;
            Q2=makeQuery(id+"F0.imprint","IMPRINT",FACE,{"disambiguationData":[TD([[makeQuery(id+"F0.imprint","IMPRINT",EDGE,{"derivedFrom":sQuery(id+"F0.wireOp",EDGE,"E36.3.0")}),1.0]])]});
            var Q3;
            Q3=makeQuery(id+"F0.imprint","IMPRINT",FACE,{"disambiguationData":[TD([[makeQuery(id+"F0.imprint","IMPRINT",EDGE,{"derivedFrom":sQuery(id+"F0.wireOp",EDGE,"E36.2.0")}),1.0]])]});
            extrude(context, id + "F2", {"entities" : qUnion([Q0, Q1, Q2, Q3]), "operationType" : NewBodyOperationType.ADD, "depth" : 15.24 * mm});
        }
        {
            var Q0;
            {var subQ0=sQuery(id+"F0.wireOp",EDGE,"E0");Q0=makeQuery(id+"F0.imprint","IMPRINT",FACE,{"disambiguationData":[TD([[makeQuery(id+"F0.imprint","IMPRINT",EDGE,{"derivedFrom":subQ0}),1.0]])]});}
            var Q1;
            {var subQ2=sQuery(id+"F0.wireOp",EDGE,"E45.trimOffspring");Q1=makeQuery(id+"F0.imprint","IMPRINT",FACE,{"disambiguationData":[TD([[makeQuery(id+"F0.imprint","IMPRINT",EDGE,{"derivedFrom":subQ2}),1.0]])]});}
            var Q2;
            {var subQ2=sQuery(id+"F0.wireOp",EDGE,"E46.trimOffspring");Q2=makeQuery(id+"F0.imprint","IMPRINT",FACE,{"disambiguationData":[TD([[makeQuery(id+"F0.imprint","IMPRINT",EDGE,{"derivedFrom":subQ2}),1.0]])]});}
            var Q3;
            {var subQ2=sQuery(id+"F0.wireOp",EDGE,"E47.trimOffspring");Q3=makeQuery(id+"F0.imprint","IMPRINT",FACE,{"disambiguationData":[TD([[makeQuery(id+"F0.imprint","IMPRINT",EDGE,{"derivedFrom":subQ2}),1.0]])]});}
            extrude(context, id + "F3", {"entities" : qUnion([Q0, Q1, Q2, Q3]), "depth" : 17.78 * mm});
        }
        {
            var Q0;
            Q0=makeQuery(id+"F3.opExtrude","CAP_FACE",FACE,{"disambiguationData":[OSD([sQuery(id+"F0.wireOp",EDGE,"E36.1.55"),sQuery(id+"F0.wireOp",EDGE,"E36.2.56"),sQuery(id+"F0.wireOp",EDGE,"E45.trimOffspring"),sQuery(id+"F0.wireOp",EDGE,"E57")])],"isStart":false});
            var sketch = newSketch(context, id + "F4", { "sketchPlane" : qUnion([Q0])});
            skCircle(sketch, "E65", {"center": v(0, 0) * mm, "radius": 9.53 * mm});
            skSolve(sketch);
        }
        {
            var Q0;
            Q0 = qSketchRegion(id + "F4", true);
            extrude(context, id + "F5", {"entities" : qUnion([Q0]), "oppositeDirection" : true, "depth" : 2.54 * mm});
        }
        {
            var Q0;
            Q0=makeQuery(id+"F5.opExtrude","CAP_FACE",FACE,{"disambiguationData":[OSD([sQuery(id+"F4.wireOp",EDGE,"E65")])],"isStart":true});
            var sketch = newSketch(context, id + "F6", { "sketchPlane" : qUnion([Q0])});
            skCircle(sketch, "E66", {"center": v(0, 0) * mm, "radius": 2.38 * mm});
            skSolve(sketch);
        }
        {
            var Q0;
            Q0=makeQuery(id+"F6.imprint","IMPRINT",FACE,{"disambiguationData":[TD([[makeQuery(id+"F6.imprint","IMPRINT",EDGE,{"derivedFrom":sQuery(id+"F6.wireOp",EDGE,"E66")}),1.0]])]});
            extrude(context, id + "F7", {"entities" : qUnion([Q0]), "operationType" : NewBodyOperationType.REMOVE, "oppositeDirection" : true, "depth" : 12.7 * mm});
        }
        {
            var Q0;
            Q0=qCreatedBy(makeId("Top.planeOp"),FACE);
            var sketch = newSketch(context, id + "F8", { "sketchPlane" : qUnion([Q0])});
            skLineSegment(sketch, "E67.0", {"start": v(-12.06, -12.07) * mm, "end": v(-53.98, -12.07) * mm});
            skArc(sketch, "E67.1", {"start": v(-62.87, -3.18) * mm, "mid": v(-60.26, -9.46) * mm, "end": v(-53.98, -12.07) * mm});
            skLineSegment(sketch, "E67.2", {"start": v(-62.87, -3.18) * mm, "end": v(-62.87, 3.18) * mm});
            skArc(sketch, "E67.3", {"start": v(-53.98, 12.07) * mm, "mid": v(-60.26, 9.46) * mm, "end": v(-62.87, 3.18) * mm});
            skLineSegment(sketch, "E67.4", {"start": v(-12.07, 12.06) * mm, "end": v(-53.98, 12.07) * mm});
            skLineSegment(sketch, "E67.5", {"start": v(-12.07, 12.06) * mm, "end": v(-12.07, 53.98) * mm});
            skArc(sketch, "E67.6", {"start": v(-3.18, 62.87) * mm, "mid": v(-9.46, 60.26) * mm, "end": v(-12.07, 53.98) * mm});
            skLineSegment(sketch, "E67.7", {"start": v(-3.18, 62.87) * mm, "end": v(3.17, 62.87) * mm});
            skArc(sketch, "E67.8", {"start": v(12.06, 53.98) * mm, "mid": v(9.46, 60.26) * mm, "end": v(3.17, 62.87) * mm});
            skLineSegment(sketch, "E67.9", {"start": v(12.06, 12.07) * mm, "end": v(12.06, 53.98) * mm});
            skLineSegment(sketch, "E67.10", {"start": v(12.06, 12.07) * mm, "end": v(53.98, 12.06) * mm});
            skArc(sketch, "E67.11", {"start": v(62.87, 3.17) * mm, "mid": v(60.26, 9.46) * mm, "end": v(53.98, 12.06) * mm});
            skLineSegment(sketch, "E67.12", {"start": v(62.87, 3.17) * mm, "end": v(62.87, -3.18) * mm});
            skArc(sketch, "E67.13", {"start": v(53.97, -12.07) * mm, "mid": v(60.26, -9.46) * mm, "end": v(62.87, -3.18) * mm});
            skLineSegment(sketch, "E67.14", {"start": v(12.07, -12.07) * mm, "end": v(53.97, -12.07) * mm});
            skLineSegment(sketch, "E67.15", {"start": v(12.07, -12.07) * mm, "end": v(12.07, -53.98) * mm});
            skArc(sketch, "E67.16", {"start": v(3.17, -62.87) * mm, "mid": v(9.46, -60.26) * mm, "end": v(12.07, -53.98) * mm});
            skLineSegment(sketch, "E67.17", {"start": v(3.17, -62.87) * mm, "end": v(-3.18, -62.87) * mm});
            skArc(sketch, "E67.18", {"start": v(-12.07, -53.98) * mm, "mid": v(-9.46, -60.26) * mm, "end": v(-3.18, -62.87) * mm});
            skLineSegment(sketch, "E67.19", {"start": v(-12.06, -12.07) * mm, "end": v(-12.07, -53.98) * mm});
            skSolve(sketch);
        }
        {
            var Q0;
            Q0 = qSketchRegion(id + "F8", true);
            extrude(context, id + "F9", {"entities" : qUnion([Q0]), "endBound" : BoundingType.SYMMETRIC, "depth" : 3.8 * mm});
        }
    });
